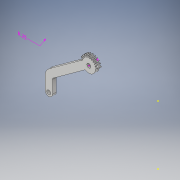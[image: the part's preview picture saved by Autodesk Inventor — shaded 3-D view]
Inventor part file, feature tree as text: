
AUTODESK INVENTOR PART (.ipt)
format: ipt  version: 2018 (Build 220112000, 112)  size: 218,624 bytes
history: native  units: in
note: dims shown in document units (in); Inventor stores cm internally (conversion verified against a paired STEP export)
features: sketch x8, extrude x4, other x2, plane x1, pattern_circular x1
ambient origin geometry x8: Origin, YZ Plane, XZ Plane, XY Plane, X Axis, Y Axis, Z Axis, Center Point
bodies: Solid1 (feature_tree)
feature tree (16):
  other  "Annotations"
  extrude  "Extrusion1"  Depth=0.1181in
  sketch  "Sketch15"  dims[d47=0.1969in d48=0.1969in d63=2.1654in d64=0.1969in]
  sketch  "Sketch16"  dims[d65=0.1969in d69=0.1094in]
  plane  "Work Plane2"
  sketch  "Sketch18"  dims[d82=0.066in]
  extrude  "Extrusion13"  Depth=2.1654in
  sketch  "Sketch20"  dims[d84=0.0098in]
  extrude  "Extrusion15"  Depth=0.1094in
  pattern_circular  "Circular Pattern2"  [2 undecoded]
  extrude  "Extrusion16"  Depth=0.1181in
  sketch  "Sketch1"  dims[d7=0.1181in d8=0.0in d15=1.0in]
  sketch  "Sketch19"  dims[d83=0.0197in]
  sketch  "Sketch21"  dims[d85=0.0394in]
  sketch  "Sketch22"  dims[d86=0.0029in d87=0.1181in d88=0.0in d94=0.1181in d95=0.1181in d96=0.0in d97=3.937in d98=-0.9757in d107=1.1811in d108=0.1181in d109=0.3937in d110=0.0in d28=1.2193in d29=0.25in]
  other  "Radial Dimension 1"
note: 2 required parameter values undecoded (feature->parameter linkage not recoverable at this tier; creation-order binding heuristic only, values carry confidence <= 0.55)
